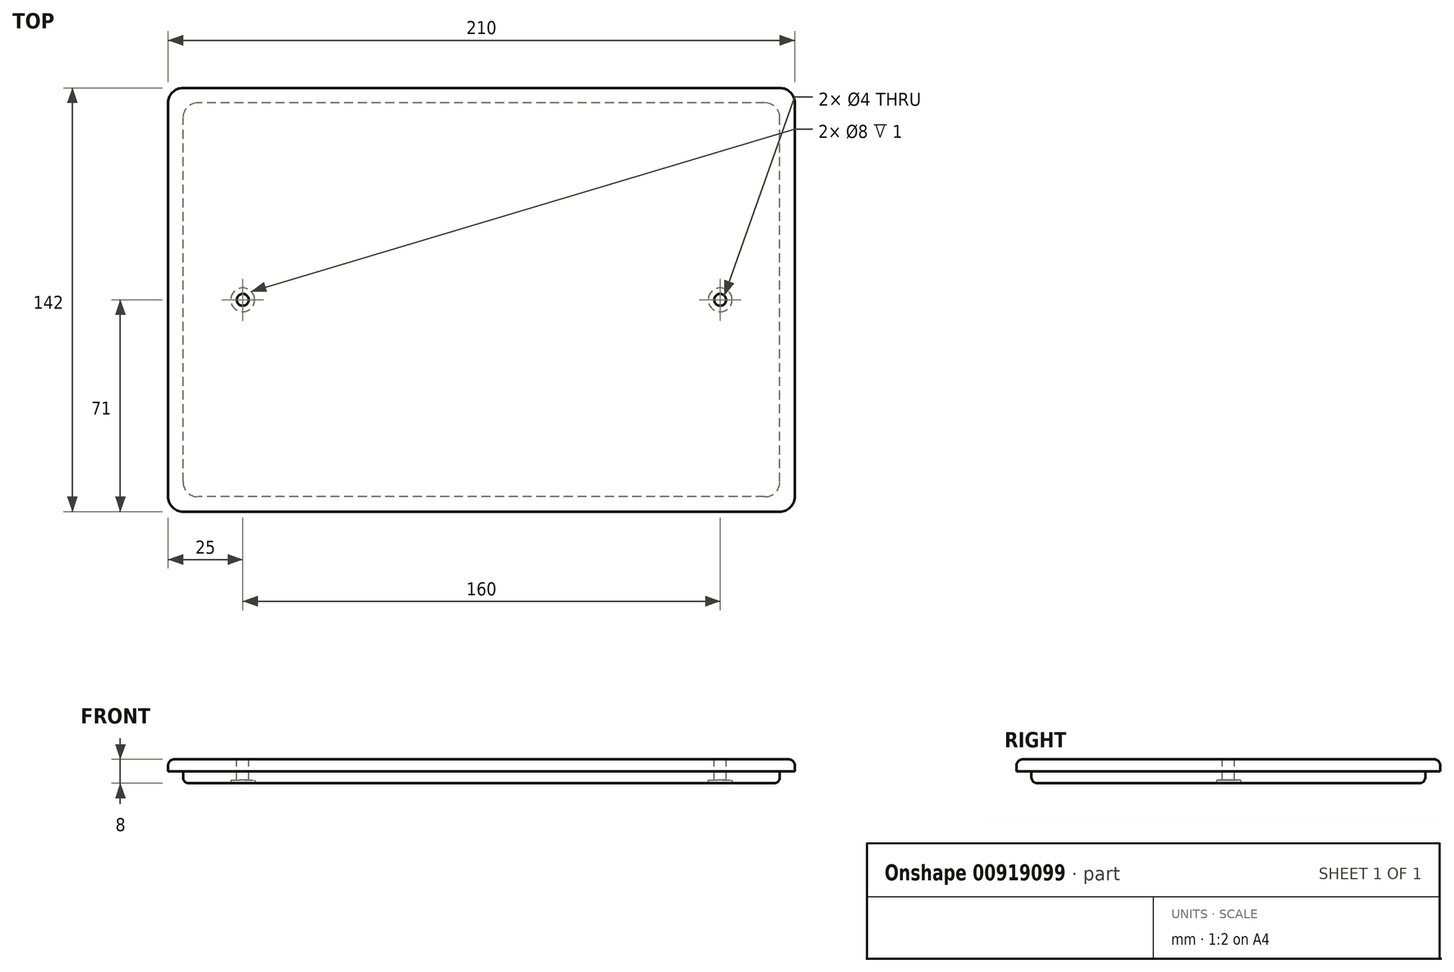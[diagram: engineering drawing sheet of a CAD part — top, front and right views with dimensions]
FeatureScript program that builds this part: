
annotation { "Feature Type Name" : "Feature", "Feature Type Description" : "" }
export const myFeature = defineFeature(function(context is Context, id is Id, definition is map)
    precondition{}
    {
        {
            var Q0;
            Q0=qCreatedBy(makeId("Top.planeOp"),FACE);
            var sketch = newSketch(context, id + "F0", { "sketchPlane" : qUnion([Q0])});
            skLineSegment(sketch, "E0.bottom", {"start": v(100, -66) * mm, "end": v(-100, -66) * mm});
            skLineSegment(sketch, "E0.top", {"start": v(100, 66) * mm, "end": v(-100, 66) * mm});
            skLineSegment(sketch, "E0.left", {"start": v(100, -66) * mm, "end": v(100, 66) * mm});
            skLineSegment(sketch, "E0.right", {"start": v(-100, -66) * mm, "end": v(-100, 66) * mm});
            skPoint(sketch, "E0.middle", {"position": v(0, 0) * mm});
            skSolve(sketch);
        }
        {
            var Q0;
            Q0=makeQuery(id+"F0.imprint","IMPRINT",FACE,{"disambiguationData":[TD([[makeQuery(id+"F0.imprint","IMPRINT",EDGE,{"derivedFrom":sQuery(id+"F0.wireOp",EDGE,"E0.bottom")}),-1.0]])]});
            extrude(context, id + "F1", {"entities" : qUnion([Q0]), "depth" : 4 * mm, "offsetDistance" : 25.4 * mm});
        }
        {
            var Q0;
            Q0=makeQuery(id+"F1.opExtrude","CAP_FACE",FACE,{"disambiguationData":[OSD([sQuery(id+"F0.wireOp",EDGE,"E0.bottom"),sQuery(id+"F0.wireOp",EDGE,"E0.top"),sQuery(id+"F0.wireOp",EDGE,"E0.left"),sQuery(id+"F0.wireOp",EDGE,"E0.right")])],"isStart":false});
            var sketch = newSketch(context, id + "F2", { "sketchPlane" : qUnion([Q0])});
            skLineSegment(sketch, "E1.bottom", {"start": v(105, -71) * mm, "end": v(-105, -71) * mm});
            skLineSegment(sketch, "E1.top", {"start": v(105, 71) * mm, "end": v(-105, 71) * mm});
            skLineSegment(sketch, "E1.left", {"start": v(105, -71) * mm, "end": v(105, 71) * mm});
            skLineSegment(sketch, "E1.right", {"start": v(-105, -71) * mm, "end": v(-105, 71) * mm});
            skPoint(sketch, "E1.middle", {"position": v(0, 0) * mm});
            skSolve(sketch);
        }
        {
            var Q0;
            Q0=makeQuery(id+"F2.imprint","IMPRINT",FACE,{"disambiguationData":[TD([[makeQuery(id+"F2.imprint","IMPRINT",EDGE,{"derivedFrom":sQuery(id+"F2.wireOp",EDGE,"E1.bottom")}),-1.0]])]});
            var Q1;
            Q1=makeQuery(id+"F2.imprint","IMPRINT",FACE,{"disambiguationData":[TD([[makeQuery(id+"F2.imprint","IMPRINT",EDGE,{"derivedFrom":makeQuery(id+"F1.opExtrude","CAP_EDGE",EDGE,{"disambiguationData":[OSD([sQuery(id+"F0.wireOp",EDGE,"E0.bottom")])],"isStart":false})}),-1.0]])]});
            extrude(context, id + "F3", {"entities" : qUnion([Q0, Q1]), "operationType" : NewBodyOperationType.ADD, "depth" : 4 * mm, "offsetDistance" : 25 * mm});
        }
        {
            var Q0;
            Q0=makeQuery(id+"F3.opExtrude","CAP_EDGE",EDGE,{"disambiguationData":[OSD([sQuery(id+"F2.wireOp",EDGE,"E1.right")])],"isStart":false});
            var Q1;
            Q1=makeQuery(id+"F3.opExtrude","CAP_EDGE",EDGE,{"disambiguationData":[OSD([sQuery(id+"F2.wireOp",EDGE,"E1.top")])],"isStart":false});
            var Q2;
            Q2=makeQuery(id+"F3.opExtrude","CAP_EDGE",EDGE,{"disambiguationData":[OSD([sQuery(id+"F2.wireOp",EDGE,"E1.left")])],"isStart":false});
            var Q3;
            Q3=makeQuery(id+"F3.opExtrude","CAP_EDGE",EDGE,{"disambiguationData":[OSD([sQuery(id+"F2.wireOp",EDGE,"E1.bottom")])],"isStart":false});
            fillet(context, id + "F4", {"entities" : qUnion([Q0, Q1, Q2, Q3]), "radius" : 2 * mm, "tangentPropagation" : true, "allowEdgeOverflow" : false});
        }
        {
            var Q0;
            Q0=makeQuery(id+"F1.opExtrude","CAP_EDGE",EDGE,{"disambiguationData":[OSD([sQuery(id+"F0.wireOp",EDGE,"E0.bottom")])],"isStart":true});
            var Q1;
            Q1=makeQuery(id+"F1.opExtrude","CAP_EDGE",EDGE,{"disambiguationData":[OSD([sQuery(id+"F0.wireOp",EDGE,"E0.left")])],"isStart":true});
            var Q2;
            Q2=makeQuery(id+"F1.opExtrude","CAP_EDGE",EDGE,{"disambiguationData":[OSD([sQuery(id+"F0.wireOp",EDGE,"E0.top")])],"isStart":true});
            var Q3;
            Q3=makeQuery(id+"F1.opExtrude","CAP_EDGE",EDGE,{"disambiguationData":[OSD([sQuery(id+"F0.wireOp",EDGE,"E0.right")])],"isStart":true});
            fillet(context, id + "F5", {"entities" : qUnion([Q0, Q1, Q2, Q3]), "radius" : 2 * mm, "tangentPropagation" : true, "allowEdgeOverflow" : false});
        }
        {
            var Q0;
            Q0=makeQuery(id+"F3.opExtrude","SWEPT_EDGE",EDGE,{"disambiguationData":[OSD([sQuery(id+"F2.wireOp",EDGE,"E1.bottom"),sQuery(id+"F2.wireOp",EDGE,"E1.left")])]});
            var Q1;
            Q1=makeQuery(id+"F1.opExtrude","SWEPT_EDGE",EDGE,{"disambiguationData":[OSD([sQuery(id+"F0.wireOp",EDGE,"E0.bottom"),sQuery(id+"F0.wireOp",EDGE,"E0.left")])]});
            var Q2;
            Q2=makeQuery(id+"F1.opExtrude","SWEPT_EDGE",EDGE,{"disambiguationData":[OSD([sQuery(id+"F0.wireOp",EDGE,"E0.top"),sQuery(id+"F0.wireOp",EDGE,"E0.left")])]});
            var Q3;
            Q3=makeQuery(id+"F3.opExtrude","SWEPT_EDGE",EDGE,{"disambiguationData":[OSD([sQuery(id+"F2.wireOp",EDGE,"E1.top"),sQuery(id+"F2.wireOp",EDGE,"E1.left")])]});
            var Q4;
            Q4=makeQuery(id+"F1.opExtrude","SWEPT_EDGE",EDGE,{"disambiguationData":[OSD([sQuery(id+"F0.wireOp",EDGE,"E0.top"),sQuery(id+"F0.wireOp",EDGE,"E0.right")])]});
            var Q5;
            Q5=makeQuery(id+"F3.opExtrude","SWEPT_EDGE",EDGE,{"disambiguationData":[OSD([sQuery(id+"F2.wireOp",EDGE,"E1.top"),sQuery(id+"F2.wireOp",EDGE,"E1.right")])]});
            var Q6;
            Q6=makeQuery(id+"F1.opExtrude","SWEPT_EDGE",EDGE,{"disambiguationData":[OSD([sQuery(id+"F0.wireOp",EDGE,"E0.bottom"),sQuery(id+"F0.wireOp",EDGE,"E0.right")])]});
            var Q7;
            Q7=makeQuery(id+"F3.opExtrude","SWEPT_EDGE",EDGE,{"disambiguationData":[OSD([sQuery(id+"F2.wireOp",EDGE,"E1.bottom"),sQuery(id+"F2.wireOp",EDGE,"E1.right")])]});
            fillet(context, id + "F6", {"entities" : qUnion([Q0, Q1, Q2, Q3, Q4, Q5, Q6, Q7]), "radius" : 5 * mm, "tangentPropagation" : true, "allowEdgeOverflow" : false});
        }
        {
            var Q0;
            Q0=makeQuery(id+"F3.opExtrude","CAP_FACE",FACE,{"disambiguationData":[OSD([sQuery(id+"F2.wireOp",EDGE,"E1.bottom"),sQuery(id+"F2.wireOp",EDGE,"E1.top"),sQuery(id+"F2.wireOp",EDGE,"E1.left"),sQuery(id+"F2.wireOp",EDGE,"E1.right")])],"isStart":false});
            var sketch = newSketch(context, id + "F7", { "sketchPlane" : qUnion([Q0])});
            skCircle(sketch, "E2", {"center": v(-80, 0) * mm, "radius": 2 * mm});
            skCircle(sketch, "E3", {"center": v(80, 0) * mm, "radius": 2 * mm});
            skSolve(sketch);
        }
        {
            var Q0;
            Q0=makeQuery(id+"F7.imprint","IMPRINT",FACE,{"disambiguationData":[TD([[makeQuery(id+"F7.imprint","IMPRINT",EDGE,{"derivedFrom":sQuery(id+"F7.wireOp",EDGE,"E2")}),1.0]])]});
            var Q1;
            Q1=makeQuery(id+"F7.imprint","IMPRINT",FACE,{"disambiguationData":[TD([[makeQuery(id+"F7.imprint","IMPRINT",EDGE,{"derivedFrom":sQuery(id+"F7.wireOp",EDGE,"E3")}),1.0]])]});
            var Q2;
            Q2=makeQuery(id+"F1.opExtrude","CAP_FACE",FACE,{"disambiguationData":[OSD([sQuery(id+"F0.wireOp",EDGE,"E0.bottom"),sQuery(id+"F0.wireOp",EDGE,"E0.top"),sQuery(id+"F0.wireOp",EDGE,"E0.left"),sQuery(id+"F0.wireOp",EDGE,"E0.right")])],"isStart":true});
            extrude(context, id + "F8", {"entities" : qUnion([Q0, Q1]), "operationType" : NewBodyOperationType.REMOVE, "endBound" : BoundingType.THROUGH_ALL, "oppositeDirection" : true, "depth" : 25 * mm, "endBoundEntityFace" : qUnion([Q2]), "offsetDistance" : 25 * mm});
        }
        {
            var Q0;
            Q0=makeQuery(id+"F1.opExtrude","CAP_FACE",FACE,{"disambiguationData":[OSD([sQuery(id+"F0.wireOp",EDGE,"E0.bottom"),sQuery(id+"F0.wireOp",EDGE,"E0.top"),sQuery(id+"F0.wireOp",EDGE,"E0.left"),sQuery(id+"F0.wireOp",EDGE,"E0.right")])],"isStart":true});
            var sketch = newSketch(context, id + "F9", { "sketchPlane" : qUnion([Q0])});
            skCircle(sketch, "E4", {"center": v(-80, 0) * mm, "radius": 4 * mm});
            skCircle(sketch, "E5", {"center": v(80, 0) * mm, "radius": 4 * mm});
            skSolve(sketch);
        }
        {
            var Q0;
            Q0=makeQuery(id+"F9.imprint","IMPRINT",FACE,{"disambiguationData":[TD([[makeQuery(id+"F9.imprint","IMPRINT",EDGE,{"derivedFrom":sQuery(id+"F9.wireOp",EDGE,"E4")}),1.0]])]});
            var Q1;
            Q1=makeQuery(id+"F9.imprint","IMPRINT",FACE,{"disambiguationData":[TD([[makeQuery(id+"F9.imprint","IMPRINT",EDGE,{"derivedFrom":sQuery(id+"F9.wireOp",EDGE,"E5")}),1.0]])]});
            extrude(context, id + "F10", {"entities" : qUnion([Q0, Q1]), "operationType" : NewBodyOperationType.REMOVE, "oppositeDirection" : true, "depth" : 1 * mm, "offsetDistance" : 25 * mm});
        }
    });
